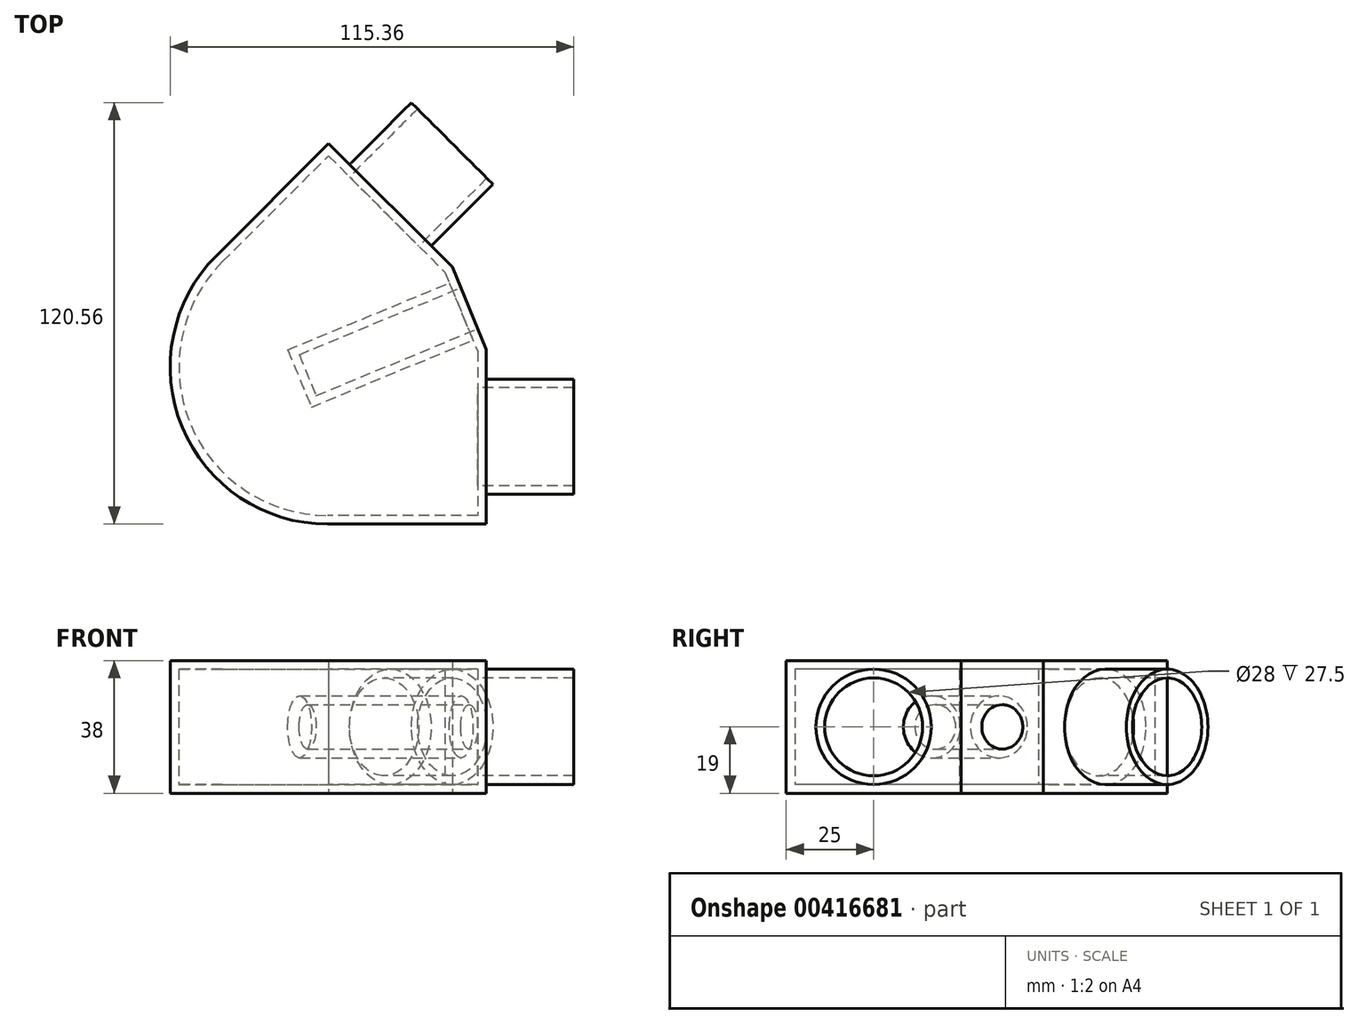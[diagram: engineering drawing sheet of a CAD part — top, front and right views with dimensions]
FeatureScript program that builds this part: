
annotation { "Feature Type Name" : "Feature", "Feature Type Description" : "" }
export const myFeature = defineFeature(function(context is Context, id is Id, definition is map)
    precondition{}
    {
        {
            var Q0;
            Q0=qCreatedBy(makeId("Top.planeOp"),FACE);
            var sketch = newSketch(context, id + "F0", { "sketchPlane" : qUnion([Q0])});
            skLineSegment(sketch, "E0", {"start": v(-23.81, 0) * mm, "end": v(85.08, 108.9) * mm});
            skLineSegment(sketch, "E1", {"start": v(130.19, 0) * mm, "end": v(-23.81, 0) * mm});
            skLineSegment(sketch, "E2", {"start": v(130.19, 50) * mm, "end": v(130.19, 0) * mm});
            skLineSegment(sketch, "E3", {"start": v(85.08, 108.9) * mm, "end": v(120.44, 73.54) * mm});
            skLineSegment(sketch, "E4", {"start": v(120.44, 73.54) * mm, "end": v(130.19, 50) * mm});
            skSolve(sketch);
        }
        {
            var Q0;
            Q0=makeQuery(id+"F0.imprint","IMPRINT",FACE,{"disambiguationData":[TD([[makeQuery(id+"F0.imprint","IMPRINT",EDGE,{"derivedFrom":sQuery(id+"F0.wireOp",EDGE,"E0")}),-1.0]])]});
            extrude(context, id + "F1", {"entities" : qUnion([Q0]), "depth" : 38 * mm});
        }
        {
            var Q0;
            Q0=makeQuery(id+"F1.opExtrude","SWEPT_FACE",FACE,{"disambiguationData":[OSD([sQuery(id+"F0.wireOp",EDGE,"E2")])]});
            var sketch = newSketch(context, id + "F2", { "sketchPlane" : qUnion([Q0])});
            skLineSegment(sketch, "E5", {"start": v(0, 19) * mm, "end": v(0, 19) * mm});
            skLineSegment(sketch, "E6", {"start": v(25, 38) * mm, "end": v(25, 0) * mm, "construction": true});
            skCircle(sketch, "E7", {"center": v(25, 19) * mm, "radius": 16.5 * mm});
            skSolve(sketch);
        }
        {
            var Q0;
            Q0=makeQuery(id+"F2.imprint","IMPRINT",FACE,{"disambiguationData":[TD([[makeQuery(id+"F2.imprint","IMPRINT",EDGE,{"derivedFrom":sQuery(id+"F2.wireOp",EDGE,"E7")}),1.0]])]});
            extrude(context, id + "F3", {"entities" : qUnion([Q0]), "operationType" : NewBodyOperationType.ADD, "depth" : 25 * mm});
        }
        {
            var Q0;
            Q0=makeQuery(id+"F1.opExtrude","SWEPT_EDGE",EDGE,{"disambiguationData":[OSD([sQuery(id+"F0.wireOp",EDGE,"E0"),sQuery(id+"F0.wireOp",EDGE,"E1")])]});
            fillet(context, id + "F4", {"entities" : qUnion([Q0]), "radius" : 45 * mm, "tangentPropagation" : true, "allowEdgeOverflow" : false});
        }
        {
            var Q0;
            Q0=makeQuery(id+"F1.opExtrude","SWEPT_FACE",FACE,{"disambiguationData":[OSD([sQuery(id+"F0.wireOp",EDGE,"E3")])]});
            var sketch = newSketch(context, id + "F5", { "sketchPlane" : qUnion([Q0])});
            skCircle(sketch, "E8", {"center": v(-8.16, 19) * mm, "radius": 16.5 * mm});
            skPoint(sketch, "E8.centerSnap0", {"position": v(-33.16, 19) * mm});
            skPoint(sketch, "E8.centerSnap1", {"position": v(-8.16, 0) * mm});
            skSolve(sketch);
        }
        {
            var Q0;
            Q0=makeQuery(id+"F5.imprint","IMPRINT",FACE,{"disambiguationData":[TD([[makeQuery(id+"F5.imprint","IMPRINT",EDGE,{"derivedFrom":sQuery(id+"F5.wireOp",EDGE,"E8")}),1.0]])]});
            extrude(context, id + "F6", {"entities" : qUnion([Q0]), "operationType" : NewBodyOperationType.ADD, "depth" : 25 * mm});
        }
        {
            var Q0;
            Q0=makeQuery(id+"F1.opExtrude","SWEPT_FACE",FACE,{"disambiguationData":[OSD([sQuery(id+"F0.wireOp",EDGE,"E4")])]});
            var sketch = newSketch(context, id + "F7", { "sketchPlane" : qUnion([Q0])});
            skCircle(sketch, "E9", {"center": v(9.11, 19) * mm, "radius": 6.35 * mm});
            skPoint(sketch, "E9.centerSnap0", {"position": v(9.11, 0) * mm});
            skPoint(sketch, "E9.centerSnap1", {"position": v(-3.63, 19) * mm});
            skSolve(sketch);
        }
        {
            var Q0;
            Q0=makeQuery(id+"F7.imprint","IMPRINT",FACE,{"disambiguationData":[TD([[makeQuery(id+"F7.imprint","IMPRINT",EDGE,{"derivedFrom":sQuery(id+"F7.wireOp",EDGE,"E9")}),1.0]])]});
            extrude(context, id + "F8", {"entities" : qUnion([Q0]), "operationType" : NewBodyOperationType.REMOVE, "oppositeDirection" : true, "depth" : 50 * mm});
        }
        {
            var Q0;
            Q0=makeQuery(id+"F3.opExtrude","CAP_FACE",FACE,{"disambiguationData":[OSD([sQuery(id+"F2.wireOp",EDGE,"E7")])],"isStart":false});
            var Q1;
            Q1=makeQuery(id+"F6.opExtrude","CAP_FACE",FACE,{"disambiguationData":[OSD([sQuery(id+"F5.wireOp",EDGE,"E8")])],"isStart":false});
            shell(context, id + "F9", {"entities" : qUnion([Q0, Q1]), "thickness" : 2.5 * mm});
        }
    });
